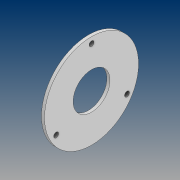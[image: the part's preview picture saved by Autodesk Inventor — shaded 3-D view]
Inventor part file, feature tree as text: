
AUTODESK INVENTOR PART (.ipt)
format: ipt  version: 2021 (Build 250183000, 183)  size: 103,936 bytes
history: native  units: mm
features: thread x3, extrude x2, sketch x2
ambient origin geometry x8: Origin, YZ Plane, XZ Plane, XY Plane, X Axis, Y Axis, Z Axis, Center Point
bodies: Solid1 (feature_tree)
feature tree (7):
  extrude  "Extrusion1"  Depth=5.0mm
  extrude  "Extrusion4"  Depth=5.0mm
  thread  "Thread1"  [1 undecoded]
  thread  "Thread5"  [1 undecoded]
  thread  "Thread6"  [1 undecoded]
  sketch  "Sketch1"  dims[d1=5.0mm d2=0.0mm d11=152.9mm d12=60.0mm]
  sketch  "Sketch3"  dims[d23=133.0mm d24=8.0mm d29=0.0mm d30=0.0mm d35=5.0mm d36=0.0mm d43=30.0mm d45=360.0deg d47=5.0mm d48=0.0mm d49=5.0mm d50=0.0mm]
note: 3 required parameter values undecoded (feature->parameter linkage not recoverable at this tier; creation-order binding heuristic only, values carry confidence <= 0.55)
